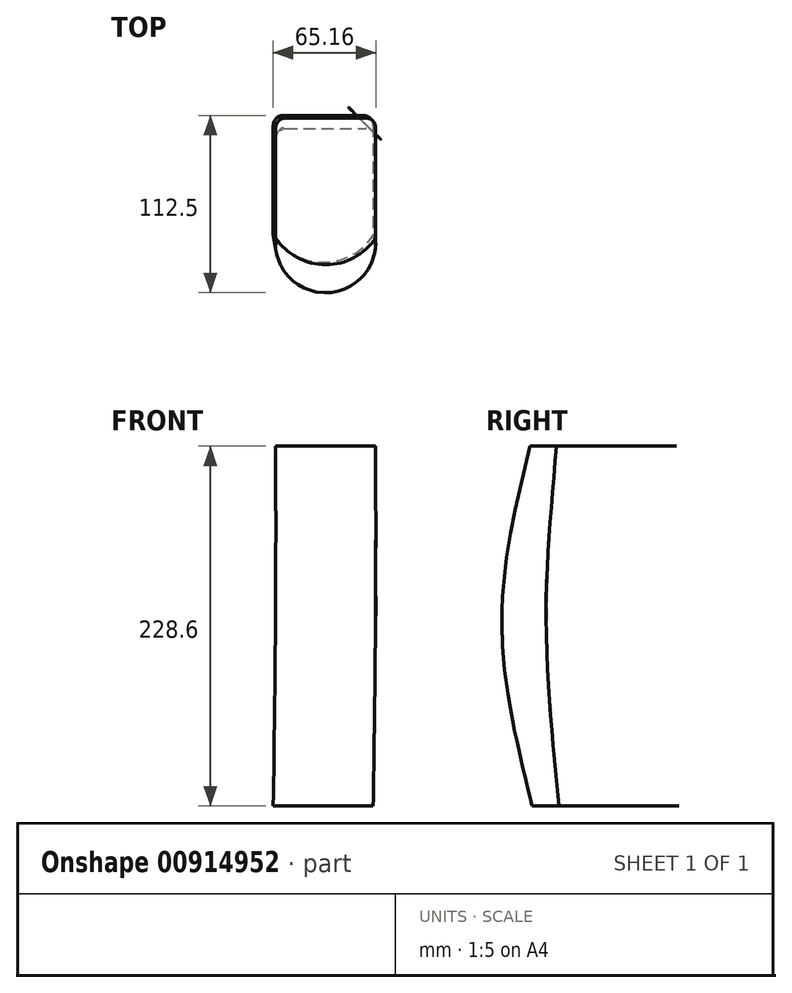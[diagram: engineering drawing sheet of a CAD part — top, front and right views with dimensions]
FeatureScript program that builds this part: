
annotation { "Feature Type Name" : "Feature", "Feature Type Description" : "" }
export const myFeature = defineFeature(function(context is Context, id is Id, definition is map)
    precondition{}
    {
        {
            var Q0;
            Q0=qCreatedBy(makeId("Top.planeOp"),FACE);
            var sketch = newSketch(context, id + "F0", { "sketchPlane" : qUnion([Q0])});
            skLineSegment(sketch, "E0", {"start": v(-45.13, 58.6) * mm, "end": v(5.67, 58.6) * mm});
            skLineSegment(sketch, "E1", {"start": v(12.02, 52.25) * mm, "end": v(12.02, -17.6) * mm});
            skLineSegment(sketch, "E2", {"start": v(-51.48, -17.6) * mm, "end": v(-51.48, 52.25) * mm});
            skArc(sketch, "E3", {"start": v(-51.48, -17.6) * mm, "mid": v(-19.73, -34.64) * mm, "end": v(12.02, -17.6) * mm});
            skPoint(sketch, "E4.visualSharp", {"position": v(-51.48, 58.6) * mm});
            skArc(sketch, "E4.filletArc", {"start": v(-45.13, 58.6) * mm, "mid": v(-49.62, 56.74) * mm, "end": v(-51.48, 52.25) * mm});
            skPoint(sketch, "E5.visualSharp", {"position": v(12.02, 58.6) * mm});
            skArc(sketch, "E5.filletArc", {"start": v(12.02, 52.25) * mm, "mid": v(10.16, 56.74) * mm, "end": v(5.67, 58.6) * mm});
            skSolve(sketch);
        }
        {
            var Q0;
            Q0=sQuery(id+"F0.wireOp",EDGE,"E3");
            cPoint(context, id + "F1", {"entities" : qUnion([Q0]), "parameter" : 0.5});
        }
        {
            var Q0;
            Q0 = qCreatedBy(id + "F1" ,VERTEX);
            var Q1;
            Q1=sQuery(id+"F0.wireOp",EDGE,"E3");
            cPlane(context, id + "F2", {"entities" : qUnion([Q0, Q1]), "cplaneType" : CPlaneType.CURVE_POINT, "offset" : 25.4 * mm, "width" : 152.4 * mm, "height" : 152.4 * mm});
        }
        {
            var Q0;
            Q0=qCreatedBy(id+"F2.planeOp",FACE);
            var sketch = newSketch(context, id + "F3", { "sketchPlane" : qUnion([Q0])});
            skFitSpline(sketch, "E6", {"points": [v(-35.87, 228.6) * mm, v(-53.14, 115.04) * mm, v(-34.63, 0) * mm], "startDerivative": vector(-61.47, -264.37) * mm, "endDerivative": vector(62.31, -261.6) * mm});
            skSolve(sketch);
        }
        {
            var Q0;
            Q0=makeQuery(id+"F0.imprint","IMPRINT",FACE,{"disambiguationData":[TD([[makeQuery(id+"F0.imprint","IMPRINT",EDGE,{"derivedFrom":sQuery(id+"F0.wireOp",EDGE,"E0")}),-1.0]])]});
            cPlane(context, id + "F4", {"entities" : qUnion([Q0]), "cplaneType" : CPlaneType.OFFSET, "offset" : 228.6 * mm, "width" : 152.4 * mm, "height" : 152.4 * mm});
        }
        {
            var Q0;
            Q0=qCreatedBy(id+"F4.planeOp",FACE);
            var sketch = newSketch(context, id + "F5", { "sketchPlane" : qUnion([Q0])});
            skLineSegment(sketch, "E7", {"start": v(-43.58, 57.07) * mm, "end": v(7.22, 57.07) * mm});
            skLineSegment(sketch, "E8", {"start": v(13.57, 50.72) * mm, "end": v(13.57, -19.13) * mm});
            skLineSegment(sketch, "E9", {"start": v(-49.93, 50.72) * mm, "end": v(-49.93, -19.13) * mm});
            skArc(sketch, "E10", {"start": v(-49.93, -19.13) * mm, "mid": v(-18.18, -36.17) * mm, "end": v(13.57, -19.13) * mm});
            skPoint(sketch, "E11.visualSharp", {"position": v(13.57, 57.07) * mm});
            skArc(sketch, "E11.filletArc", {"start": v(13.57, 50.72) * mm, "mid": v(11.7, 55.21) * mm, "end": v(7.22, 57.07) * mm});
            skPoint(sketch, "E12.visualSharp", {"position": v(-49.93, 57.07) * mm});
            skArc(sketch, "E12.filletArc", {"start": v(-43.58, 57.07) * mm, "mid": v(-48.07, 55.21) * mm, "end": v(-49.93, 50.72) * mm});
            skSolve(sketch);
        }
        {
            var Q0;
            Q0=makeQuery(id+"F0.imprint","IMPRINT",FACE,{"disambiguationData":[TD([[makeQuery(id+"F0.imprint","IMPRINT",EDGE,{"derivedFrom":sQuery(id+"F0.wireOp",EDGE,"E0")}),-1.0]])]});
            cPlane(context, id + "F6", {"entities" : qUnion([Q0]), "cplaneType" : CPlaneType.OFFSET, "offset" : 114.3 * mm, "width" : 152.4 * mm, "height" : 152.4 * mm});
        }
        {
            var Q0;
            Q0=qCreatedBy(id+"F6.planeOp",FACE);
            var sketch = newSketch(context, id + "F7", { "sketchPlane" : qUnion([Q0])});
            skLineSegment(sketch, "E13", {"start": v(7.07, 50.45) * mm, "end": v(-43.73, 50.45) * mm});
            skLineSegment(sketch, "E14", {"start": v(-50.08, 44.1) * mm, "end": v(-50.08, -25.75) * mm});
            skLineSegment(sketch, "E15", {"start": v(13.42, 44.1) * mm, "end": v(13.42, -25.75) * mm});
            skPoint(sketch, "E16.visualSharp", {"position": v(-50.08, 50.45) * mm});
            skArc(sketch, "E16.filletArc", {"start": v(-43.73, 50.45) * mm, "mid": v(-48.22, 48.59) * mm, "end": v(-50.08, 44.1) * mm});
            skPoint(sketch, "E17.visualSharp", {"position": v(13.42, 50.45) * mm});
            skArc(sketch, "E17.filletArc", {"start": v(13.42, 44.1) * mm, "mid": v(11.56, 48.59) * mm, "end": v(7.07, 50.45) * mm});
            skArc(sketch, "E18", {"start": v(-50.08, -25.33) * mm, "mid": v(-18.52, -53.88) * mm, "end": v(13.42, -25.75) * mm});
            skSolve(sketch);
        }
        {
            var Q0;
            Q0=sQuery(id+"F3.wireOp",EDGE,"E6");
            var Q1;
            Q1=makeQuery(id+"F5.imprint","IMPRINT",FACE,{"disambiguationData":[TD([[makeQuery(id+"F5.imprint","IMPRINT",EDGE,{"derivedFrom":sQuery(id+"F5.wireOp",EDGE,"E7")}),-1.0]])]});
            var Q2;
            Q2=makeQuery(id+"F7.imprint","IMPRINT",FACE,{"disambiguationData":[TD([[makeQuery(id+"F7.imprint","IMPRINT",EDGE,{"derivedFrom":sQuery(id+"F7.wireOp",EDGE,"E13")}),1.0]])]});
            var Q3;
            Q3=makeQuery(id+"F0.imprint","IMPRINT",FACE,{"disambiguationData":[TD([[makeQuery(id+"F0.imprint","IMPRINT",EDGE,{"derivedFrom":sQuery(id+"F0.wireOp",EDGE,"E0")}),-1.0]])]});
            loft(context, id + "F8", {"addSections" : true, "spine" : qUnion([Q0]), "sectionCount" : 5, "sheetProfilesArray" : [{ "sheetProfileEntities" : qUnion([Q1]) }, { "sheetProfileEntities" : qUnion([Q2]) }, { "sheetProfileEntities" : qUnion([Q3]) }]});
        }
    });
